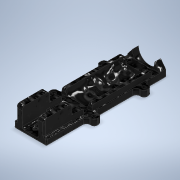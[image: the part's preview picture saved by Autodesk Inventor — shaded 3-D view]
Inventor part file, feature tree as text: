
AUTODESK INVENTOR PART (.ipt)
format: ipt  version: 2020 (Build 240168000, 168)  size: 729,088 bytes
history: native  units: mm
features: projected_geometry x17, sketch x15, extrude x14, fillet x6, hole x2, chamfer x2, plane x1, direct_edit x1, move_body x1
ambient origin geometry x8: Origin, YZ Plane, XZ Plane, XY Plane, X Axis, Y Axis, Z Axis, Center Point
bodies: Solid1 (feature_tree)
feature tree (59):
  extrude  "Extrusion1"  Depth=29.0mm
  plane  "Work Plane1"
  sketch  "Sketch2"  dims[d2=6.0mm d3=0.0mm d4=-7.0mm]
  extrude  "Extrusion2"  [1 undecoded]
  extrude  "Extrusion7"  Depth=21.5mm
  extrude  "Extrusion3"  Depth=12.5mm
  hole  "Hole1"  [1 undecoded]
  direct_edit  "Direct Edit1"
  extrude  "Extrusion4"  Depth=5.0mm
  extrude  "Extrusion5"  Depth=5.0mm
  extrude  "Extrusion6"  Depth=5.0mm
  hole  "Hole2"  [1 undecoded]
  extrude  "Extrusion8"  Depth=31.0mm TaperAngle=0.0deg
  fillet  "Fillet1"  Radius=10.5mm
  fillet  "Fillet2"  Radius=31.0mm
  fillet  "Fillet3"  Radius=3.0mm
  chamfer  "Chamfer1"  Distance=14.0mm
  chamfer  "Chamfer2"  Distance=7.0mm
  fillet  "Fillet4"  Radius=7.0mm
  extrude  "Extrusion9"  Depth=7.0mm
  fillet  "Fillet5"  Radius=6.0mm
  extrude  "Extrusion10"  Depth=0.15mm
  extrude  "Extrusion11"  Depth=0.15mm
  extrude  "Extrusion12"  Depth=0.15mm
  extrude  "Extrusion13"  Depth=0.15mm
  fillet  "Fillet6"  Radius=31.0mm
  extrude  "Extrusion14"  Depth=0.15mm
  sketch  "Sketch1"  dims[d0=29.0mm d1=100.0mm]
  projected_geometry  "Projected Loop1"
  sketch  "Sketch3"  dims[d5=12.5mm d6=21.5mm]
  projected_geometry  "Projected Loop2"
  sketch  "Sketch4"  dims[d7=51.8mm d8=0.0mm d9=12.5mm]
  projected_geometry  "Projected Loop3"
  sketch  "Sketch5"  dims[d10=20.0mm d11=34.0mm d12=0.0mm]
  projected_geometry  "Projected Loop4"
  sketch  "Sketch6"  dims[d13=3.0mm d14=5.0mm]
  projected_geometry  "Projected Loop5"
  sketch  "Sketch7"  dims[d15=3.0mm d16=5.0mm]
  projected_geometry  "Projected Loop6"
  sketch  "Sketch8"  dims[d17=3.1mm d18=6.0mm d19=5.5mm d20=2.0mm d21=90.0deg d22=6.0mm d23=0.0mm d24=5.0mm]
  projected_geometry  "Projected Loop7"
  sketch  "Sketch9"  dims[d25=63.0mm d26=5.0mm]
  projected_geometry  "Projected Loop8"
  sketch  "Sketch10"  dims[d27=63.0mm d28=0.0mm d29=0.0mm d30=31.0mm d31=10.5mm d32=31.0mm d33=3.0mm d34=0.0mm]
  projected_geometry  "Projected Loop9"
  sketch  "Sketch11"  dims[d35=5.0mm]
  projected_geometry  "Projected Loop10"
  sketch  "Sketch12"  dims[d36=20.0mm]
  projected_geometry  "Projected Loop11"
  projected_geometry  "Projected Loop12"
  projected_geometry  "Projected Loop13"
  sketch  "Sketch14"  dims[d37=5.0mm]
  sketch  "Sketch16"  dims[d38=20.0mm d39=14.0mm d40=0.0mm]
  projected_geometry  "Projected Loop22"
  sketch  "Sketch17"  dims[d41=7.0mm d42=7.0mm d43=7.0mm d44=7.0mm d45=6.0mm d46=0.0mm d47=3.5mm d48=3.5mm d49=3.5mm d50=3.5mm d51=3.1mm d52=6.0mm d53=5.5mm d54=2.0mm d55=90.0deg d56=6.0mm d57=0.0mm d58=31.0mm d59=38.0mm d60=34.0mm d61=6.75mm d62=0.0mm d63=55.0mm d64=176.0mm d65=152.0mm d66=85.25mm d67=0.0mm d68=1.0mm d69=3.0mm d70=3.0mm d71=3.0mm d72=1.0mm d73=4.5mm d74=6.0mm d75=45.0deg d76=4.5mm d77=6.0mm d78=45.0deg d79=1.0mm d80=5.0mm d81=0.0mm d82=3.0mm d83=1.0mm d84=6.1mm d85=27.2mm d87=14.5mm d88=53.8mm d89=0.1mm d90=0.1mm d91=5.0mm d92=0.0mm d93=5.0mm d94=53.75mm d95=0.0mm d96=0.0mm d98=15.0mm d99=0.0mm d100=17.25mm d101=0.0mm d102=2.0mm d103=0.15mm d104=0.15mm d105=0.15mm d106=0.15mm d107=0.0mm d108=17.25mm d109=0.0mm]
  projected_geometry  "Projected Loop23"
  projected_geometry  "Projected Loop24"
  projected_geometry  "Projected Loop25"
  move_body  "Move1"
note: 3 required parameter values undecoded (feature->parameter linkage not recoverable at this tier; creation-order binding heuristic only, values carry confidence <= 0.55)
